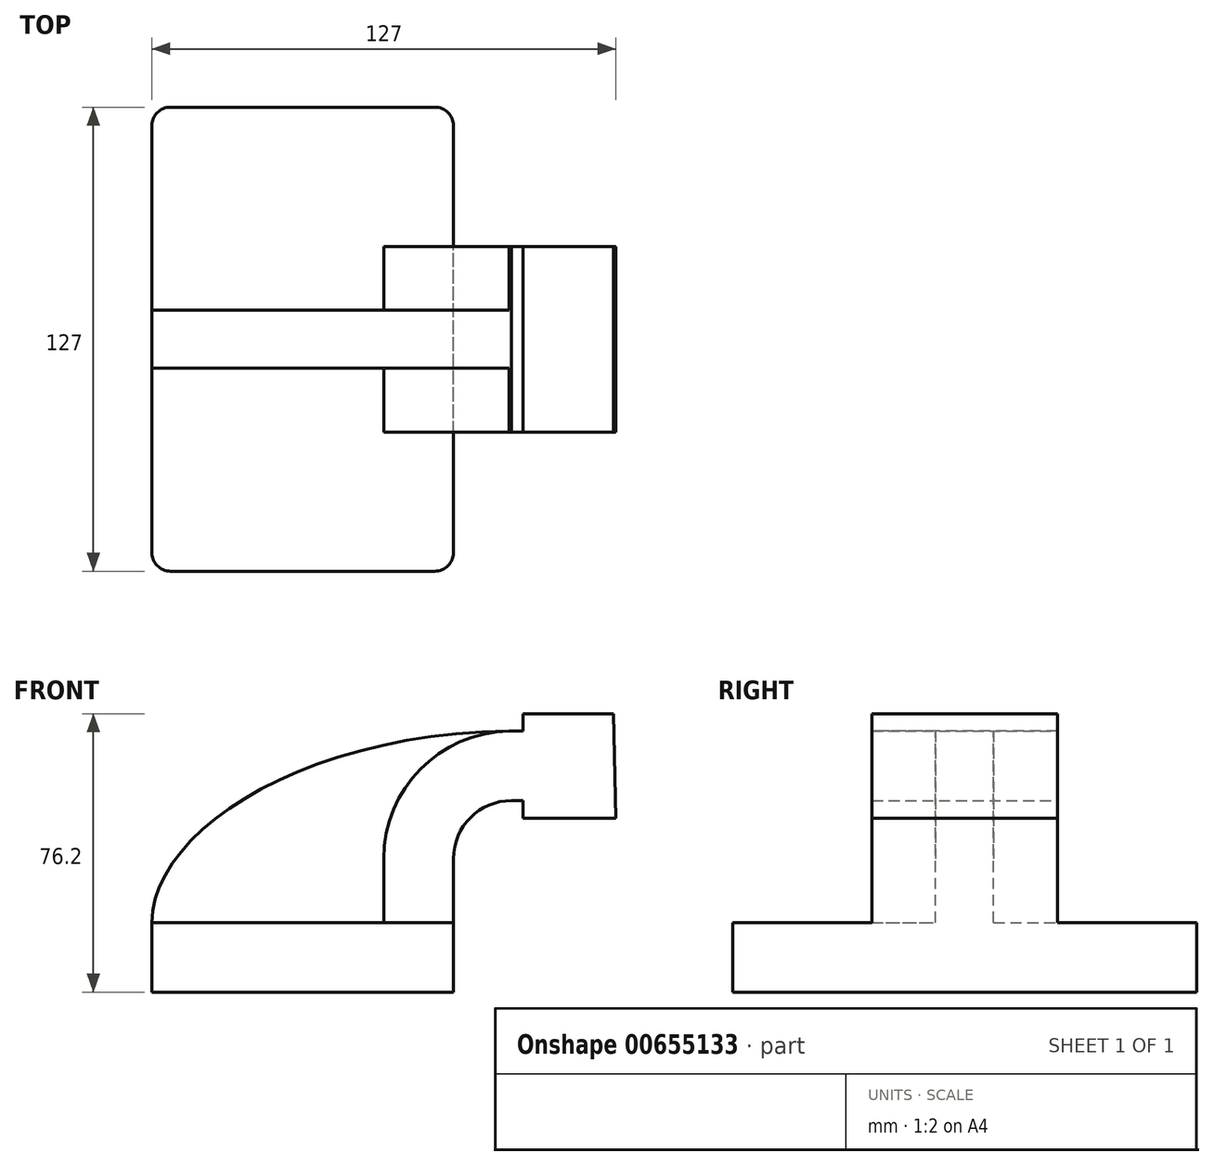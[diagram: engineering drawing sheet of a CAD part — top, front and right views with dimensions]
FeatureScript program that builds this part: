
annotation { "Feature Type Name" : "Feature", "Feature Type Description" : "" }
export const myFeature = defineFeature(function(context is Context, id is Id, definition is map)
    precondition{}
    {
        {
            var Q0;
            Q0=qCreatedBy(makeId("Front.planeOp"),FACE);
            var sketch = newSketch(context, id + "F0", { "sketchPlane" : qUnion([Q0])});
            skLineSegment(sketch, "E0.bottom", {"start": v(-41.28, -9.53) * mm, "end": v(41.28, -9.53) * mm});
            skLineSegment(sketch, "E0.top", {"start": v(-41.28, 9.53) * mm, "end": v(41.28, 9.53) * mm});
            skLineSegment(sketch, "E0.left", {"start": v(-41.28, -9.53) * mm, "end": v(-41.28, 9.53) * mm});
            skLineSegment(sketch, "E0.right", {"start": v(41.28, -9.53) * mm, "end": v(41.28, 9.53) * mm});
            skPoint(sketch, "E0.middle", {"position": v(0, 0) * mm});
            skLineSegment(sketch, "E1.bottom", {"start": v(60.32, 66.67) * mm, "end": v(111.12, 66.67) * mm});
            skLineSegment(sketch, "E1.top", {"start": v(60.33, 38.1) * mm, "end": v(111.12, 38.1) * mm});
            skLineSegment(sketch, "E1.left", {"start": v(60.32, 66.67) * mm, "end": v(60.33, 38.1) * mm});
            skLineSegment(sketch, "E1.right", {"start": v(111.12, 66.67) * mm, "end": v(111.12, 38.1) * mm});
            skPoint(sketch, "E1.middle", {"position": v(85.72, 52.39) * mm});
            skLineSegment(sketch, "E2", {"start": v(41.28, 9.53) * mm, "end": v(41.28, 27) * mm});
            skArc(sketch, "E3", {"start": v(41.27, 27) * mm, "mid": v(45.92, 38.23) * mm, "end": v(57.15, 42.88) * mm});
            skLineSegment(sketch, "E4", {"start": v(57.15, 42.88) * mm, "end": v(85.09, 42.88) * mm});
            skLineSegment(sketch, "E5.0", {"start": v(57.15, 61.93) * mm, "end": v(85.09, 61.93) * mm});
            skArc(sketch, "E5.1", {"start": v(22.22, 27) * mm, "mid": v(32.45, 51.7) * mm, "end": v(57.15, 61.93) * mm});
            skLineSegment(sketch, "E5.2", {"start": v(22.22, 9.53) * mm, "end": v(22.22, 27) * mm});
            skLineSegment(sketch, "E6", {"start": v(85.72, 38.1) * mm, "end": v(85.09, 66.67) * mm});
            skFitSpline(sketch, "E7", {"points": [v(-41.28, 9.53) * mm, v(57.15, 61.93) * mm], "startDerivative": vector(0.26, 74.49) * mm, "endDerivative": vector(171.45, 1.4) * mm});
            skSolve(sketch);
        }
        {
            var Q0;
            Q0=makeQuery(id+"F0.imprint","IMPRINT",FACE,{"disambiguationData":[TD([[makeQuery(id+"F0.imprint","IMPRINT",EDGE,{"derivedFrom":sQuery(id+"F0.wireOp",EDGE,"E0.bottom")}),1.0]])]});
            extrude(context, id + "F1", {"entities" : qUnion([Q0]), "endBound" : BoundingType.SYMMETRIC, "depth" : 127 * mm, "offsetDistance" : 25.4 * mm});
        }
        {
            var Q0;
            {var subQ1=sQuery(id+"F0.wireOp",EDGE,"E2");Q0=makeQuery(id+"F0.imprint","IMPRINT",FACE,{"disambiguationData":[TD([[makeQuery(id+"F0.imprint","IMPRINT",EDGE,{"derivedFrom":subQ1}),1.0]])]});}
            var Q1;
            {var subQ4=sQuery(id+"F0.wireOp",EDGE,"E6");Q1=makeQuery(id+"F0.imprint","IMPRINT",FACE,{"disambiguationData":[TD([[makeQuery(id+"F0.imprint","IMPRINT",EDGE,{"derivedFrom":subQ4}),1.0]])]});}
            extrude(context, id + "F2", {"entities" : qUnion([Q0, Q1]), "operationType" : NewBodyOperationType.ADD, "endBound" : BoundingType.SYMMETRIC, "depth" : 50.8 * mm, "offsetDistance" : 25.4 * mm});
        }
        {
            var Q0;
            {var subQ3=sQuery(id+"F0.wireOp",EDGE,"E5.2");Q0=makeQuery(id+"F0.imprint","IMPRINT",FACE,{"disambiguationData":[TD([[makeQuery(id+"F0.imprint","IMPRINT",EDGE,{"derivedFrom":subQ3}),1.0]])]});}
            extrude(context, id + "F3", {"entities" : qUnion([Q0]), "operationType" : NewBodyOperationType.ADD, "endBound" : BoundingType.SYMMETRIC, "depth" : 15.88 * mm, "offsetDistance" : 25.4 * mm});
        }
        {
            var Q0;
            Q0=makeQuery(id+"F1.opExtrude","CAP_EDGE",EDGE,{"disambiguationData":[OSD([sQuery(id+"F0.wireOp",EDGE,"E0.right")])],"isStart":false});
            var Q1;
            Q1=makeQuery(id+"F1.opExtrude","CAP_EDGE",EDGE,{"disambiguationData":[OSD([sQuery(id+"F0.wireOp",EDGE,"E0.left")])],"isStart":false});
            var Q2;
            Q2=makeQuery(id+"F1.opExtrude","CAP_EDGE",EDGE,{"disambiguationData":[OSD([sQuery(id+"F0.wireOp",EDGE,"E0.right")])],"isStart":true});
            var Q3;
            Q3=makeQuery(id+"F1.opExtrude","CAP_EDGE",EDGE,{"disambiguationData":[OSD([sQuery(id+"F0.wireOp",EDGE,"E0.left")])],"isStart":true});
            fillet(context, id + "F4", {"entities" : qUnion([Q0, Q1, Q2, Q3]), "radius" : 5.08 * mm, "tangentPropagation" : true, "allowEdgeOverflow" : false});
        }
    });
